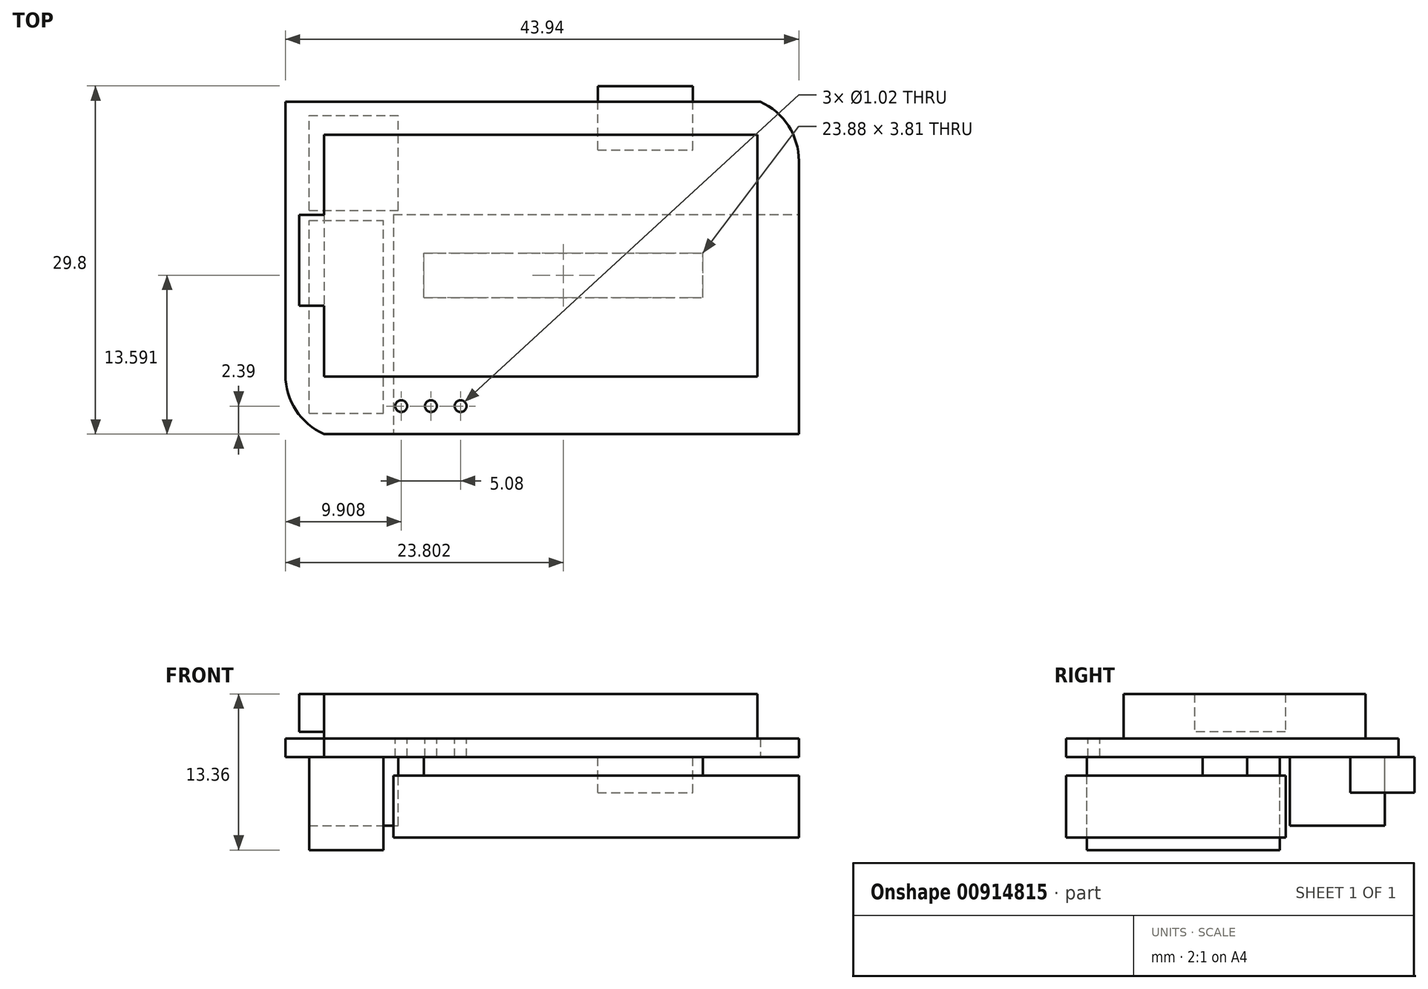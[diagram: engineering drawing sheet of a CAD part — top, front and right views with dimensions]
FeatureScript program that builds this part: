
annotation { "Feature Type Name" : "Feature", "Feature Type Description" : "" }
export const myFeature = defineFeature(function(context is Context, id is Id, definition is map)
    precondition{}
    {
        {
            var Q0;
            Q0=qCreatedBy(makeId("Top.planeOp"),FACE);
            var sketch = newSketch(context, id + "F0", { "sketchPlane" : qUnion([Q0])});
            skLineSegment(sketch, "E0.bottom", {"start": v(-3.35, -4.24) * mm, "end": v(37.3, -4.24) * mm});
            skLineSegment(sketch, "E0.top", {"start": v(-0.05, -32.69) * mm, "end": v(40.6, -32.69) * mm});
            skLineSegment(sketch, "E0.left", {"start": v(-3.35, -4.24) * mm, "end": v(-3.35, -27.6) * mm});
            skLineSegment(sketch, "E0.right", {"start": v(40.6, -9.32) * mm, "end": v(40.6, -32.69) * mm});
            skArc(sketch, "E1", {"start": v(-3.35, -27.6) * mm, "mid": v(-2.45, -30.64) * mm, "end": v(-0.05, -32.69) * mm});
            skPoint(sketch, "E2.start.orphan", {"position": v(40.6, -9.32) * mm});
            skArc(sketch, "E3", {"start": v(40.6, -9.32) * mm, "mid": v(39.7, -6.3) * mm, "end": v(37.3, -4.24) * mm});
            skSolve(sketch);
        }
        {
            var Q0;
            Q0 = qSketchRegion(id + "F0", true);
            extrude(context, id + "F1", {"entities" : qUnion([Q0]), "depth" : 1.6 * mm, "offsetDistance" : 25.4 * mm});
        }
        {
            var Q0;
            Q0=makeQuery(id+"F1.opExtrude","CAP_FACE",FACE,{"disambiguationData":[OSD([sQuery(id+"F0.wireOp",EDGE,"E0.bottom"),sQuery(id+"F0.wireOp",EDGE,"E0.top"),sQuery(id+"F0.wireOp",EDGE,"E0.left"),sQuery(id+"F0.wireOp",EDGE,"E0.right"),sQuery(id+"F0.wireOp",EDGE,"E2"),sQuery(id+"F0.wireOp",EDGE,"d4qmq6Bf-P1eI-lomc-O2O5-3S2DW3wJuivS")])],"isStart":false});
            var sketch = newSketch(context, id + "F2", { "sketchPlane" : qUnion([Q0])});
            skLineSegment(sketch, "E4.bottom", {"start": v(-0.05, -7.06) * mm, "end": v(37.04, -7.06) * mm});
            skLineSegment(sketch, "E4.top", {"start": v(-0.05, -27.76) * mm, "end": v(37.04, -27.76) * mm});
            skLineSegment(sketch, "E4.left", {"start": v(-0.05, -7.06) * mm, "end": v(-0.05, -27.76) * mm});
            skLineSegment(sketch, "E4.right", {"start": v(37.04, -7.06) * mm, "end": v(37.04, -27.76) * mm});
            skSolve(sketch);
        }
        {
            var Q0;
            Q0 = qSketchRegion(id + "F2", true);
            var Q1;
            Q1=makeQuery(id+"F2.imprint","IMPRINT",FACE,{"disambiguationData":[TD([[makeQuery(id+"F2.imprint","IMPRINT",EDGE,{"derivedFrom":sQuery(id+"F2.wireOp",EDGE,"E4.bottom")}),-1.0]])]});
            extrude(context, id + "F3", {"entities" : qUnion([Q0, Q1]), "operationType" : NewBodyOperationType.ADD, "depth" : 3.8 * mm, "offsetDistance" : 25.4 * mm});
        }
        {
            var Q0;
            Q0=makeQuery(id+"F3.opExtrude","SWEPT_FACE",FACE,{"disambiguationData":[OSD([sQuery(id+"F2.wireOp",EDGE,"E4.left")])]});
            var sketch = newSketch(context, id + "F4", { "sketchPlane" : qUnion([Q0])});
            skLineSegment(sketch, "E5.bottom", {"start": v(13.92, 5.41) * mm, "end": v(21.72, 5.41) * mm});
            skLineSegment(sketch, "E5.top", {"start": v(13.92, 2.16) * mm, "end": v(21.72, 2.16) * mm});
            skLineSegment(sketch, "E5.left", {"start": v(13.92, 5.41) * mm, "end": v(13.92, 2.16) * mm});
            skLineSegment(sketch, "E5.right", {"start": v(21.72, 5.41) * mm, "end": v(21.72, 2.16) * mm});
            skSolve(sketch);
        }
        {
            var Q0;
            Q0=makeQuery(id+"F4.imprint","IMPRINT",FACE,{"disambiguationData":[TD([[makeQuery(id+"F4.imprint","IMPRINT",EDGE,{"derivedFrom":sQuery(id+"F4.wireOp",EDGE,"E5.bottom")}),-1.0]])]});
            extrude(context, id + "F5", {"entities" : qUnion([Q0]), "operationType" : NewBodyOperationType.ADD, "depth" : 2.12 * mm, "offsetDistance" : 25.4 * mm});
        }
        {
            var Q0;
            Q0=makeQuery(id+"F1.opExtrude","CAP_FACE",FACE,{"disambiguationData":[OSD([sQuery(id+"F0.wireOp",EDGE,"E0.bottom"),sQuery(id+"F0.wireOp",EDGE,"E0.top"),sQuery(id+"F0.wireOp",EDGE,"E0.left"),sQuery(id+"F0.wireOp",EDGE,"E0.right"),sQuery(id+"F0.wireOp",EDGE,"E2"),sQuery(id+"F0.wireOp",EDGE,"d4qmq6Bf-P1eI-lomc-O2O5-3S2DW3wJuivS")])],"isStart":false});
            var sketch = newSketch(context, id + "F6", { "sketchPlane" : qUnion([Q0])});
            skCircle(sketch, "E6", {"center": v(6.56, -30.3) * mm, "radius": 0.5 * mm});
            skCircle(sketch, "E7", {"center": v(9.1, -30.3) * mm, "radius": 0.5 * mm});
            skCircle(sketch, "E8", {"center": v(11.64, -30.3) * mm, "radius": 0.5 * mm});
            skSolve(sketch);
        }
        {
            var Q0;
            Q0 = qSketchRegion(id + "F6", true);
            extrude(context, id + "F7", {"entities" : qUnion([Q0]), "operationType" : NewBodyOperationType.REMOVE, "oppositeDirection" : true, "depth" : 25.4 * mm, "offsetDistance" : 25.4 * mm});
        }
        {
            var Q0;
            Q0=makeQuery(id+"F1.opExtrude","CAP_FACE",FACE,{"disambiguationData":[OSD([sQuery(id+"F0.wireOp",EDGE,"E0.bottom"),sQuery(id+"F0.wireOp",EDGE,"E0.top"),sQuery(id+"F0.wireOp",EDGE,"E0.left"),sQuery(id+"F0.wireOp",EDGE,"E0.right"),sQuery(id+"F0.wireOp",EDGE,"E1"),sQuery(id+"F0.wireOp",EDGE,"E3")])],"isStart":true});
            var sketch = newSketch(context, id + "F8", { "sketchPlane" : qUnion([Q0])});
            skLineSegment(sketch, "E9.bottom", {"start": v(-1.32, 30.9) * mm, "end": v(5.03, 30.9) * mm});
            skLineSegment(sketch, "E9.top", {"start": v(-1.32, 14.4) * mm, "end": v(5.03, 14.4) * mm});
            skLineSegment(sketch, "E9.left", {"start": v(-1.32, 30.9) * mm, "end": v(-1.32, 14.4) * mm});
            skLineSegment(sketch, "E9.right", {"start": v(5.03, 30.9) * mm, "end": v(5.03, 14.4) * mm});
            skSolve(sketch);
        }
        {
            var Q0;
            Q0=makeQuery(id+"F8.imprint","IMPRINT",FACE,{"disambiguationData":[TD([[makeQuery(id+"F8.imprint","IMPRINT",EDGE,{"derivedFrom":sQuery(id+"F8.wireOp",EDGE,"E9.bottom")}),-1.0]])]});
            extrude(context, id + "F9", {"entities" : qUnion([Q0]), "operationType" : NewBodyOperationType.ADD, "depth" : 7.95 * mm, "offsetDistance" : 25.4 * mm});
        }
        {
            var Q0;
            Q0=makeQuery(id+"F1.opExtrude","CAP_FACE",FACE,{"disambiguationData":[OSD([sQuery(id+"F0.wireOp",EDGE,"E0.bottom"),sQuery(id+"F0.wireOp",EDGE,"E0.top"),sQuery(id+"F0.wireOp",EDGE,"E0.left"),sQuery(id+"F0.wireOp",EDGE,"E0.right"),sQuery(id+"F0.wireOp",EDGE,"E1"),sQuery(id+"F0.wireOp",EDGE,"E3")])],"isStart":true});
            var sketch = newSketch(context, id + "F10", { "sketchPlane" : qUnion([Q0])});
            skLineSegment(sketch, "E10.bottom", {"start": v(-1.32, 13.54) * mm, "end": v(6.3, 13.54) * mm});
            skLineSegment(sketch, "E10.top", {"start": v(-1.32, 5.4) * mm, "end": v(6.3, 5.4) * mm});
            skLineSegment(sketch, "E10.left", {"start": v(-1.32, 13.54) * mm, "end": v(-1.32, 5.4) * mm});
            skLineSegment(sketch, "E10.right", {"start": v(6.3, 13.54) * mm, "end": v(6.3, 5.4) * mm});
            skSolve(sketch);
        }
        {
            var Q0;
            Q0 = qSketchRegion(id + "F10", true);
            extrude(context, id + "F11", {"entities" : qUnion([Q0]), "operationType" : NewBodyOperationType.ADD, "depth" : 5.87 * mm, "offsetDistance" : 25.4 * mm});
        }
        {
            var Q0;
            Q0=makeQuery(id+"F1.opExtrude","CAP_FACE",FACE,{"disambiguationData":[OSD([sQuery(id+"F0.wireOp",EDGE,"E0.bottom"),sQuery(id+"F0.wireOp",EDGE,"E0.top"),sQuery(id+"F0.wireOp",EDGE,"E0.left"),sQuery(id+"F0.wireOp",EDGE,"E0.right"),sQuery(id+"F0.wireOp",EDGE,"E1"),sQuery(id+"F0.wireOp",EDGE,"E3")])],"isStart":true});
            var sketch = newSketch(context, id + "F12", { "sketchPlane" : qUnion([Q0])});
            skLineSegment(sketch, "E11.bottom", {"start": v(8.51, 21) * mm, "end": v(32.39, 21) * mm});
            skLineSegment(sketch, "E11.top", {"start": v(8.51, 17.2) * mm, "end": v(32.39, 17.2) * mm});
            skLineSegment(sketch, "E11.left", {"start": v(8.51, 21) * mm, "end": v(8.51, 17.2) * mm});
            skLineSegment(sketch, "E11.right", {"start": v(32.39, 21) * mm, "end": v(32.39, 17.2) * mm});
            skSolve(sketch);
        }
        {
            var Q0;
            Q0=makeQuery(id+"F12.imprint","IMPRINT",FACE,{"disambiguationData":[TD([[makeQuery(id+"F12.imprint","IMPRINT",EDGE,{"derivedFrom":sQuery(id+"F12.wireOp",EDGE,"E11.bottom")}),-1.0]])]});
            extrude(context, id + "F13", {"entities" : qUnion([Q0]), "operationType" : NewBodyOperationType.ADD, "depth" : 1.59 * mm, "offsetDistance" : 25.4 * mm});
        }
        {
            var Q0;
            Q0=makeQuery(id+"F1.opExtrude","CAP_FACE",FACE,{"disambiguationData":[OSD([sQuery(id+"F0.wireOp",EDGE,"E0.bottom"),sQuery(id+"F0.wireOp",EDGE,"E0.top"),sQuery(id+"F0.wireOp",EDGE,"E0.left"),sQuery(id+"F0.wireOp",EDGE,"E0.right"),sQuery(id+"F0.wireOp",EDGE,"E1"),sQuery(id+"F0.wireOp",EDGE,"E3")])],"isStart":true});
            var sketch = newSketch(context, id + "F14", { "sketchPlane" : qUnion([Q0])});
            skLineSegment(sketch, "E12.bottom", {"start": v(23.39, 8.37) * mm, "end": v(31.51, 8.37) * mm});
            skLineSegment(sketch, "E12.top", {"start": v(23.39, 2.9) * mm, "end": v(31.51, 2.9) * mm});
            skLineSegment(sketch, "E12.left", {"start": v(23.39, 8.37) * mm, "end": v(23.39, 2.9) * mm});
            skLineSegment(sketch, "E12.right", {"start": v(31.51, 8.37) * mm, "end": v(31.51, 2.9) * mm});
            skSolve(sketch);
        }
        {
            var Q0;
            Q0 = qSketchRegion(id + "F14", true);
            var Q1;
            {var subQ0=sQuery(id+"F14.wireOp",EDGE,"E12.bottom");Q1=makeQuery(id+"F14.imprint","IMPRINT",FACE,{"disambiguationData":[TD([[makeQuery(id+"F14.imprint","IMPRINT",EDGE,{"derivedFrom":subQ0}),-1.0]])]});}
            extrude(context, id + "F15", {"entities" : qUnion([Q0, Q1]), "operationType" : NewBodyOperationType.ADD, "depth" : 3.05 * mm, "offsetDistance" : 25.4 * mm});
        }
        {
            var Q0;
            Q0=makeQuery(id+"F13.opExtrude","CAP_FACE",FACE,{"disambiguationData":[OSD([sQuery(id+"F12.wireOp",EDGE,"E11.bottom"),sQuery(id+"F12.wireOp",EDGE,"E11.top"),sQuery(id+"F12.wireOp",EDGE,"E11.left"),sQuery(id+"F12.wireOp",EDGE,"E11.right")])],"isStart":false});
            var sketch = newSketch(context, id + "F16", { "sketchPlane" : qUnion([Q0])});
            skLineSegment(sketch, "E13.bottom", {"start": v(5.9, 13.9) * mm, "end": v(40.6, 13.9) * mm});
            skLineSegment(sketch, "E13.top", {"start": v(5.9, 32.69) * mm, "end": v(40.6, 32.69) * mm});
            skLineSegment(sketch, "E13.left", {"start": v(5.9, 13.9) * mm, "end": v(5.9, 32.69) * mm});
            skLineSegment(sketch, "E13.right", {"start": v(40.6, 13.9) * mm, "end": v(40.6, 32.69) * mm});
            skSolve(sketch);
        }
        {
            var Q0;
            Q0 = qSketchRegion(id + "F16", true);
            var Q1;
            Q1=makeQuery(id+"F16.imprint","IMPRINT",FACE,{"disambiguationData":[TD([[makeQuery(id+"F16.imprint","IMPRINT",EDGE,{"derivedFrom":sQuery(id+"F16.wireOp",EDGE,"E13.bottom")}),1.0]])]});
            extrude(context, id + "F17", {"entities" : qUnion([Q0, Q1]), "operationType" : NewBodyOperationType.ADD, "depth" : 5.3 * mm, "offsetDistance" : 25.4 * mm});
        }
    });
